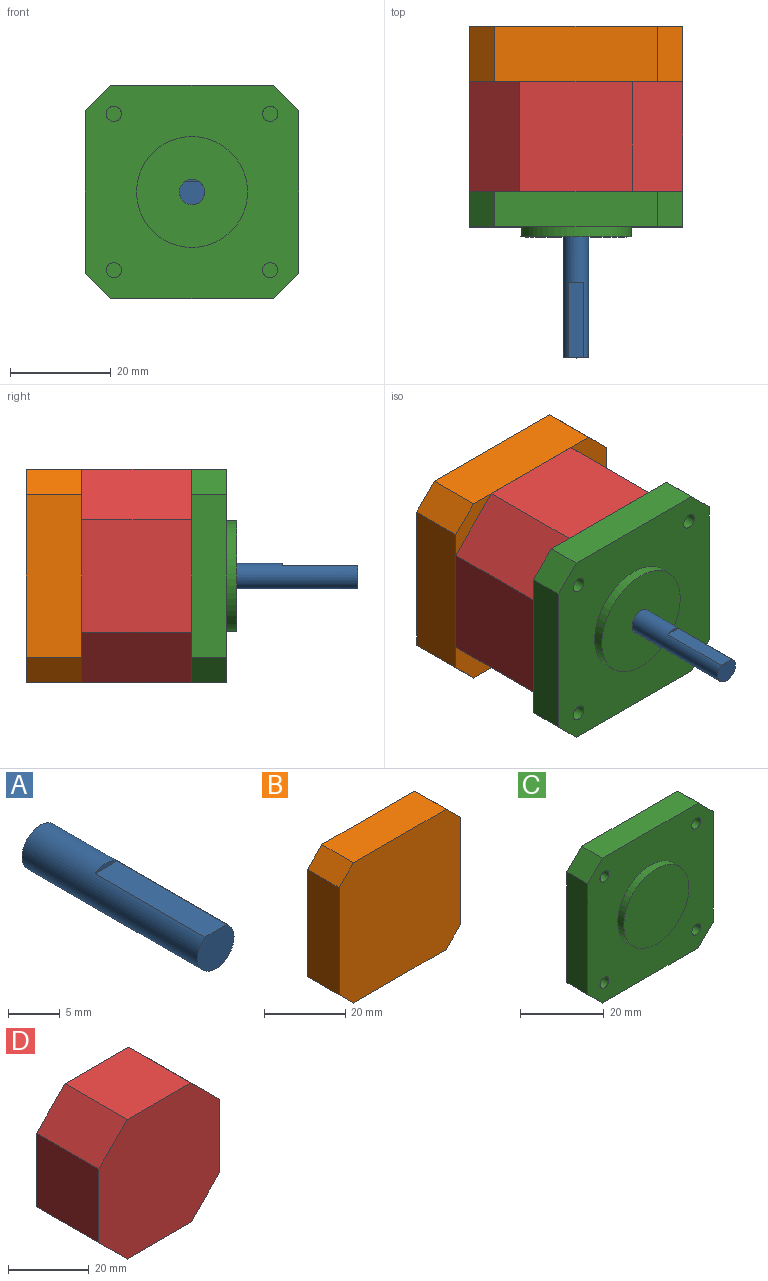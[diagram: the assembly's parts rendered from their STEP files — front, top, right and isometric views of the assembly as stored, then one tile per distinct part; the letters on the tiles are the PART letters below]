
ASSEMBLY  parts=4 mates=3
PART A: 5 faces, bbox 5x24x5 mm
  f0: cylinder r=2.5mm len=24mm, axis (0,1,0), area 328.7mm2, adj f1,f2,f3,f4
  f1: plane 5x4.5mm, normal (0,-1,0), area 18.6mm2, adj f0,f3
  f2: plane 5x5mm, normal (0,1,0), area 19.6mm2, adj f0
  f3: plane 15x3mm, normal (0,0,1), area 45mm2, adj f0,f1,f4
  f4: plane 3x0.5mm, normal (0,-1,0), area 1mm2, adj f0,f3
PART B: 18 faces, bbox 42.3x11x42.3 mm
  f0: plane 32.3x11mm, normal (1,0,0), area 355.3mm2, adj f4,f5,f8,f9
  f1: plane 32.3x11mm, normal (0,0,-1), area 355.3mm2, adj f4,f5,f7,f8
  f2: plane 32.3x11mm, normal (-1,0,0), area 355.3mm2, adj f4,f5,f6,f7
  f3: plane 32.3x11mm, normal (0,0,1), area 355.3mm2, adj f4,f5,f6,f9
  f4: plane 42.3x42.3mm, normal (0,1,0), area 1711mm2, adj f0,f1,f2,f3,f6,f7,f8,f9
  f5: plane 42.3x42.3mm, normal (0,-1,0), area 1739.3mm2, adj f0,f1,f2,f3,f6,f7,f8,f9
  f6: plane 11x5mm, normal (-0.71,0,0.71), area 77.8mm2, adj f2,f3,f4,f5
  f7: plane 11x5mm, normal (-0.71,0,-0.71), area 77.8mm2, adj f1,f2,f4,f5
  f8: plane 11x5mm, normal (0.71,0,-0.71), area 77.8mm2, adj f0,f1,f4,f5
  f9: plane 11x5mm, normal (0.71,0,0.71), area 77.8mm2, adj f0,f3,f4,f5
  f10: cylinder r=1.5mm len=4.5mm, axis (0,1,0), area 42.4mm2, adj f4,f11
  f11: plane 3x3mm, normal (0,1,0), area 7.1mm2, adj f10
  f12: cylinder r=1.5mm len=4.5mm, axis (0,1,0), area 42.4mm2, adj f4,f13
  f13: plane 3x3mm, normal (0,1,0), area 7.1mm2, adj f12
  f14: cylinder r=1.5mm len=4.5mm, axis (0,1,0), area 42.4mm2, adj f4,f15
  f15: plane 3x3mm, normal (0,1,0), area 7.1mm2, adj f14
  f16: cylinder r=1.5mm len=4.5mm, axis (0,1,0), area 42.4mm2, adj f4,f17
  f17: plane 3x3mm, normal (0,1,0), area 7.1mm2, adj f16
PART C: 20 faces, bbox 42.3x9x42.3 mm
  f0: plane 42.3x42.3mm, normal (0,-1,0), area 1330.9mm2, adj f1,f2,f3,f4,f6,f7,f8,f9
  f1: plane 32.3x7mm, normal (-1,0,0), area 226.1mm2, adj f0,f5,f6,f9
  f2: plane 32.3x7mm, normal (0,0,-1), area 226.1mm2, adj f0,f5,f6,f7
  f3: plane 32.3x7mm, normal (1,0,0), area 226.1mm2, adj f0,f5,f7,f8
  f4: plane 32.3x7mm, normal (0,0,1), area 226.1mm2, adj f0,f5,f8,f9
  f5: plane 42.3x42.3mm, normal (0,1,0), area 1739.3mm2, adj f1,f2,f3,f4,f6,f7,f8,f9
  f6: plane 7x5mm, normal (-0.71,0,-0.71), area 49.5mm2, adj f0,f1,f2,f5
  f7: plane 7x5mm, normal (0.71,0,-0.71), area 49.5mm2, adj f0,f2,f3,f5
  f8: plane 7x5mm, normal (0.71,0,0.71), area 49.5mm2, adj f0,f3,f4,f5
  f9: plane 7x5mm, normal (-0.71,0,0.71), area 49.5mm2, adj f0,f1,f4,f5
  f10: cylinder r=11mm len=22mm, axis (0,1,0), area 138.2mm2, adj f0,f11
  f11: plane 22x22mm, normal (0,-1,0), area 380.1mm2, adj f10
  f12: cylinder r=1.5mm len=4.5mm, axis (0,-1,0), area 42.4mm2, adj f0,f13
  f13: plane 3x3mm, normal (0,-1,0), area 7.1mm2, adj f12
  f14: cylinder r=1.5mm len=4.5mm, axis (0,-1,0), area 42.4mm2, adj f0,f15
  f15: plane 3x3mm, normal (0,-1,0), area 7.1mm2, adj f14
  f16: cylinder r=1.5mm len=4.5mm, axis (0,-1,0), area 42.4mm2, adj f0,f17
  f17: plane 3x3mm, normal (0,-1,0), area 7.1mm2, adj f16
  f18: cylinder r=1.5mm len=4.5mm, axis (0,-1,0), area 42.4mm2, adj f0,f19
  f19: plane 3x3mm, normal (0,-1,0), area 7.1mm2, adj f18
PART D: 10 faces, bbox 42.3x21.8x42.3 mm
  f0: plane 21.8x10mm, normal (0.71,0,0.71), area 308.3mm2, adj f3,f6,f7,f8
  f1: plane 21.8x10mm, normal (0.71,0,-0.71), area 308.3mm2, adj f3,f4,f6,f7
  f2: plane 21.8x10mm, normal (-0.71,0,0.71), area 308.3mm2, adj f6,f7,f8,f9
  f3: plane 22.3x21.8mm, normal (1,0,0), area 486.1mm2, adj f0,f1,f6,f7
  f4: plane 22.3x21.8mm, normal (0,0,-1), area 486.1mm2, adj f1,f5,f6,f7
  f5: plane 21.8x10mm, normal (-0.71,0,-0.71), area 308.3mm2, adj f4,f6,f7,f9
  f6: plane 42.3x42.3mm, normal (0,-1,0), area 1589.3mm2, adj f0,f1,f2,f3,f4,f5,f8,f9
  f7: plane 42.3x42.3mm, normal (0,1,0), area 1589.3mm2, adj f0,f1,f2,f3,f4,f5,f8,f9
  f8: plane 22.3x21.8mm, normal (0,0,1), area 486.1mm2, adj f0,f2,f6,f7
  f9: plane 22.3x21.8mm, normal (-1,0,0), area 486.1mm2, adj f2,f5,f6,f7
PLACE A t=(68.82,56.66,21.18)mm
PLACE B t=(68.82,56.66,21.18)mm
PLACE C t=(68.82,56.66,21.18)mm
PLACE D t=(68.82,56.66,21.18)mm
MATE fastened D.f6 <-> C.f10  axis (0,-1,0) through (50.37,56.66,34.61)mm
MATE revolute C.f10 <-> A.f0  axis (0,-1,0) through (50.37,47.66,34.61)mm
MATE fastened D.f7 <-> B.f5  axis (0,1,0) through (50.37,78.46,34.61)mm
